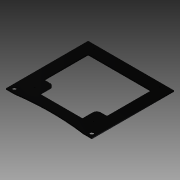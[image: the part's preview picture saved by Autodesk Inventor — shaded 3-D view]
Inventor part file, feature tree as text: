
AUTODESK INVENTOR PART (.ipt)
format: ipt  version: 2013 (Build 170138000, 138)  size: 463,872 bytes
history: native  units: mm
features: extrude x12, sketch x12, mirror x6, reference x5, fillet x2, projected_geometry x1
ambient origin geometry x8: Origin, YZ Plane, XZ Plane, XY Plane, X Axis, Y Axis, Z Axis, Center Point
bodies: Solid1 (feature_tree)
feature tree (38):
  extrude  "Extrusion1"  Depth=385.0mm
  extrude  "Extrusion2"  Depth=70.0mm
  extrude  "Extrusion3"  TaperAngle=135.0deg  [1 undecoded]
  mirror  "Mirror1"
  mirror  "Mirror2"
  extrude  "Extrusion4"  Depth=315.0mm
  mirror  "Mirror3"
  extrude  "Extrusion5"  Depth=4.0mm
  extrude  "Extrusion6"  Depth=8.0mm
  fillet  "Fillet1"  Radius=290.0mm
  fillet  "Fillet2"  Radius=8.5mm
  extrude  "Extrusion7"  Depth=75.0mm
  mirror  "Mirror4"
  extrude  "Extrusion8"  Depth=162.5mm
  mirror  "Mirror5"
  extrude  "Extrusion10"  Depth=260.0mm
  extrude  "Extrusion11"  Depth=10.0mm TaperAngle=0.0deg
  mirror  "Mirror6"
  extrude  "Extrusion14"  Depth=5.0mm
  extrude  "Extrusion15"  Depth=22.0mm
  sketch  "Sketch1"  dims[d0=270.0mm d2=385.0mm]
  sketch  "Sketch2"  dims[d3=70.0mm d4=70.0mm]
  projected_geometry  "Projected Loop1"
  sketch  "Sketch3"  dims[d6=6.477mm d7=0.0mm d8=135.0deg]
  sketch  "Sketch4"  dims[d9=8.0mm d11=315.0mm]
  sketch  "Sketch5"  dims[d12=290.0mm d13=0.0mm d14=4.0mm]
  sketch  "Sketch6"  dims[d16=1.5mm d17=8.0mm d18=290.0mm d19=0.0mm d20=8.5mm]
  sketch  "Sketch7"  dims[d21=8.0mm d22=75.0mm]
  sketch  "Sketch8"  dims[d23=10.0mm d24=0.0mm d25=162.5mm]
  sketch  "Sketch10"  dims[d26=10.0mm d27=0.0mm d28=260.0mm]
  sketch  "Sketch11"  dims[d30=87.5mm d31=10.0mm d32=0.0mm]
  sketch  "Sketch14"  dims[d33=25.0mm d34=5.0mm]
  reference  "Reference4"
  reference  "Reference5"
  reference  "Reference6"
  reference  "Reference7"
  reference  "Reference8"
  sketch  "Sketch15"  dims[d35=52.0mm d36=22.0mm d37=31.0mm d38=3.0mm d39=10.0mm d40=0.0mm d41=32.0mm d43=13.5mm d45=8.0mm d46=10.0mm d47=0.0mm d53=50.0mm d54=50.0mm d55=6.477mm d56=25.0mm d57=25.0mm d58=6.477mm d59=25.0mm d60=25.0mm d61=10.0mm d62=0.0mm d63=2.5mm d64=4.0mm d65=1.5mm d66=2.5mm d67=10.0mm d68=0.0mm d76=2.5mm d77=1.5mm d78=4.0mm d79=1.5mm d80=4.0mm d81=1.5mm d82=4.0mm d83=2.5mm d84=1.5mm d85=4.0mm d86=1.5mm d87=4.0mm d88=10.0mm d89=0.0mm d90=10.0mm d92=7.5mm d93=10.0mm d94=0.0mm]
note: 1 required parameter value undecoded (feature->parameter linkage not recoverable at this tier; creation-order binding heuristic only, values carry confidence <= 0.55)
